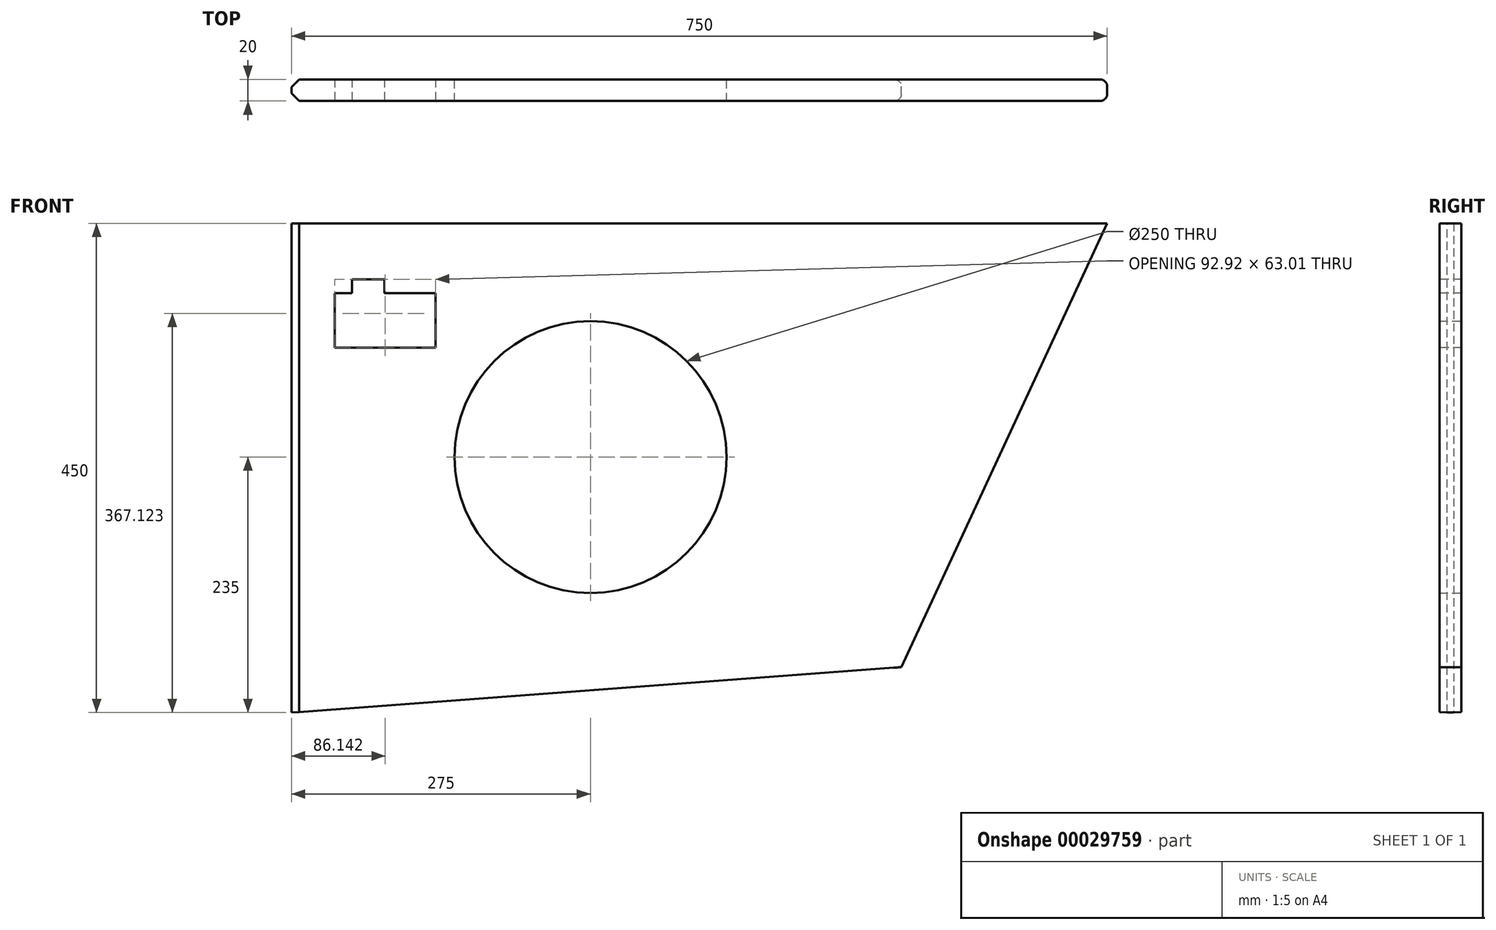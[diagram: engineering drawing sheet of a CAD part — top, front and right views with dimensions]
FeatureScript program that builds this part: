
annotation { "Feature Type Name" : "Feature", "Feature Type Description" : "" }
export const myFeature = defineFeature(function(context is Context, id is Id, definition is map)
    precondition{}
    {
        {
            var Q0;
            Q0=qCreatedBy(makeId("Front.planeOp"),FACE);
            var sketch = newSketch(context, id + "F0", { "sketchPlane" : qUnion([Q0])});
            skCircle(sketch, "E0", {"center": v(0, 0) * mm, "radius": 125 * mm});
            skLineSegment(sketch, "E1", {"start": v(-275, 215) * mm, "end": v(475, 215) * mm});
            skLineSegment(sketch, "E2", {"start": v(475, 215) * mm, "end": v(285.77, -193.28) * mm});
            skLineSegment(sketch, "E3", {"start": v(285.77, -193.28) * mm, "end": v(-275, -235) * mm});
            skLineSegment(sketch, "E4", {"start": v(-275, -235) * mm, "end": v(-275, 215) * mm});
            skSolve(sketch);
        }
        {
            var Q0;
            Q0=makeQuery(id+"F0.imprint","IMPRINT",FACE,{"disambiguationData":[TD([[makeQuery(id+"F0.imprint","IMPRINT",EDGE,{"derivedFrom":sQuery(id+"F0.wireOp",EDGE,"E0")}),-1.0]])]});
            extrude(context, id + "F1", {"entities" : qUnion([Q0]), "depth" : 20 * mm});
        }
        {
            var Q0;
            Q0=makeQuery(id+"F1.opExtrude","CAP_EDGE",EDGE,{"disambiguationData":[OSD([sQuery(id+"F0.wireOp",EDGE,"E2")])],"isStart":true});
            var Q1;
            Q1=makeQuery(id+"F1.opExtrude","CAP_EDGE",EDGE,{"disambiguationData":[OSD([sQuery(id+"F0.wireOp",EDGE,"E2")])],"isStart":false});
            fillet(context, id + "F2", {"entities" : qUnion([Q0, Q1]), "radius" : 6 * mm, "tangentPropagation" : true, "allowEdgeOverflow" : false});
        }
        {
            var Q0;
            Q0=makeQuery(id+"F1.opExtrude","CAP_EDGE",EDGE,{"disambiguationData":[OSD([sQuery(id+"F0.wireOp",EDGE,"E4")])],"isStart":false});
            chamfer(context, id + "F3", {"entities" : qUnion([Q0]), "width" : 7 * mm, "tangentPropagation" : true});
        }
        {
            var Q0;
            Q0=makeQuery(id+"F1.opExtrude","CAP_EDGE",EDGE,{"disambiguationData":[OSD([sQuery(id+"F0.wireOp",EDGE,"E4")])],"isStart":true});
            chamfer(context, id + "F4", {"entities" : qUnion([Q0]), "width" : 7 * mm, "tangentPropagation" : true});
        }
        {
            var Q0;
            Q0=makeQuery(id+"F1.opExtrude","CAP_FACE",FACE,{"disambiguationData":[OSD([sQuery(id+"F0.wireOp",EDGE,"E0"),sQuery(id+"F0.wireOp",EDGE,"E1"),sQuery(id+"F0.wireOp",EDGE,"E2"),sQuery(id+"F0.wireOp",EDGE,"E3"),sQuery(id+"F0.wireOp",EDGE,"E4")])],"isStart":false});
            var sketch = newSketch(context, id + "F5", { "sketchPlane" : qUnion([Q0])});
            skLineSegment(sketch, "E5.bottom", {"start": v(-235.32, 150.9) * mm, "end": v(-219.4, 150.9) * mm});
            skLineSegment(sketch, "E5.top", {"start": v(-235.32, 100.62) * mm, "end": v(-142.4, 100.62) * mm});
            skLineSegment(sketch, "E5.left", {"start": v(-235.32, 150.9) * mm, "end": v(-235.32, 100.62) * mm});
            skLineSegment(sketch, "E5.right", {"start": v(-142.4, 150.9) * mm, "end": v(-142.4, 100.62) * mm});
            skLineSegment(sketch, "E6.top", {"start": v(-219.4, 163.63) * mm, "end": v(-189.5, 163.63) * mm});
            skLineSegment(sketch, "E6.left", {"start": v(-219.4, 150.9) * mm, "end": v(-219.4, 163.63) * mm});
            skLineSegment(sketch, "E6.right", {"start": v(-189.5, 150.9) * mm, "end": v(-189.5, 163.63) * mm});
            skLineSegment(sketch, "E7.trimOffspring", {"start": v(-189.5, 150.9) * mm, "end": v(-142.4, 150.9) * mm});
            skSolve(sketch);
        }
        {
            var Q0;
            Q0 = qSketchRegion(id + "F5", true);
            extrude(context, id + "F6", {"entities" : qUnion([Q0]), "operationType" : NewBodyOperationType.REMOVE, "endBound" : BoundingType.THROUGH_ALL, "oppositeDirection" : true, "depth" : 25 * mm});
        }
    });
